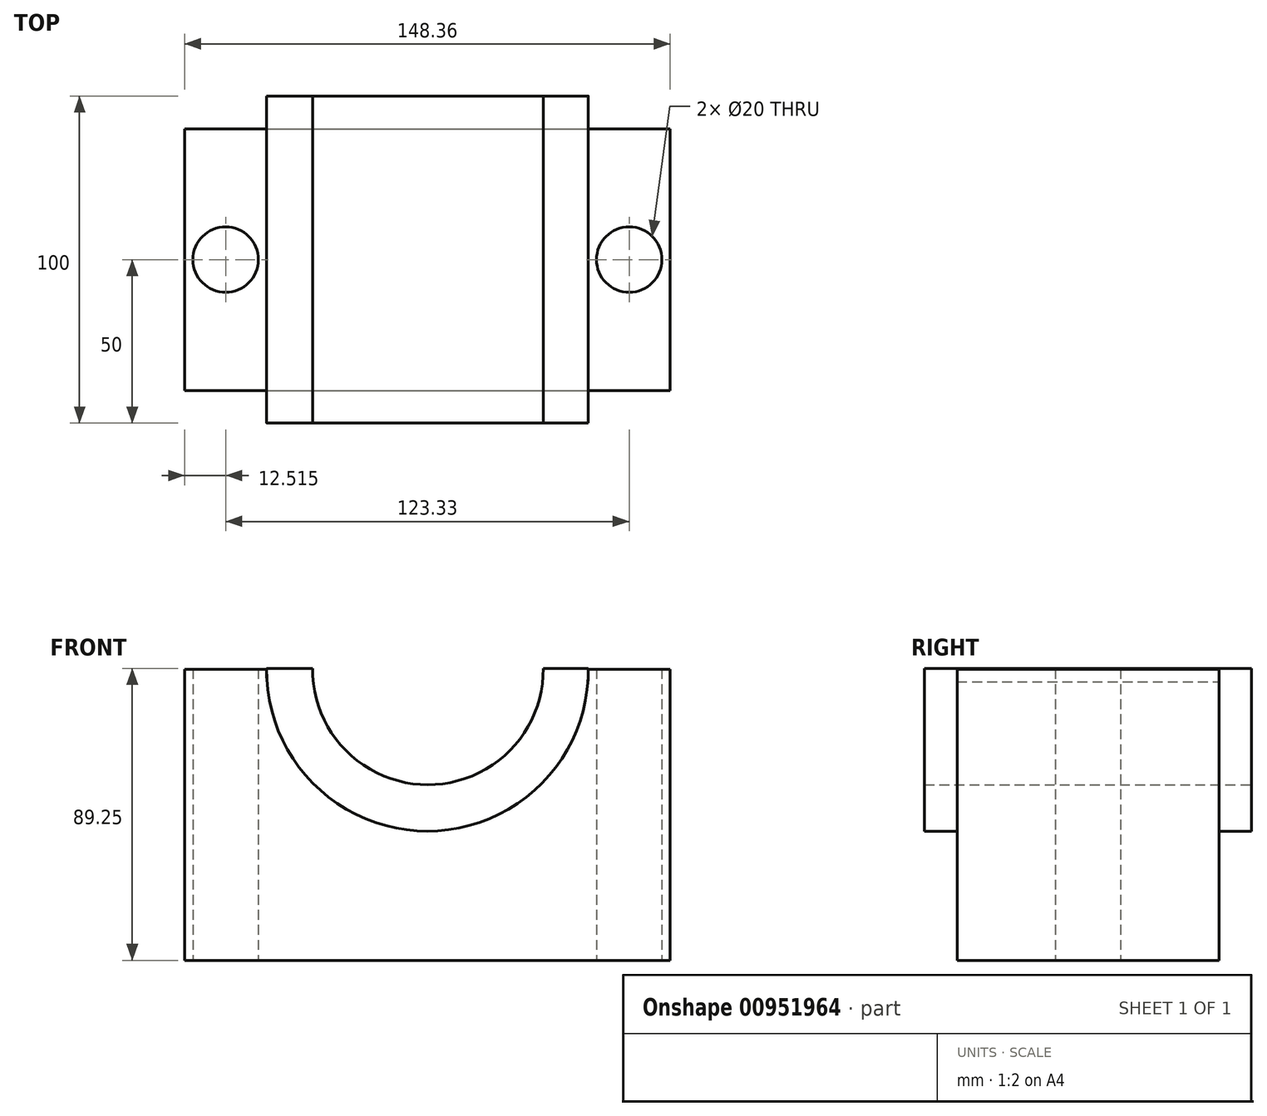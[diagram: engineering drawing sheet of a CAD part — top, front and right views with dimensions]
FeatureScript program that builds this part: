
annotation { "Feature Type Name" : "Feature", "Feature Type Description" : "" }
export const myFeature = defineFeature(function(context is Context, id is Id, definition is map)
    precondition{}
    {
        {
            var Q0;
            Q0=qCreatedBy(makeId("Front.planeOp"),FACE);
            var sketch = newSketch(context, id + "F0", { "sketchPlane" : qUnion([Q0])});
            skLineSegment(sketch, "E0.top", {"start": v(-74.18, -44.5) * mm, "end": v(74.18, -44.5) * mm});
            skLineSegment(sketch, "E0.left", {"start": v(-74.18, 44.5) * mm, "end": v(-74.18, -44.5) * mm});
            skLineSegment(sketch, "E0.right", {"start": v(74.18, 44.5) * mm, "end": v(74.18, -44.5) * mm});
            skArc(sketch, "E1", {"start": v(-35.24, 44.5) * mm, "mid": v(0, 9.26) * mm, "end": v(35.24, 44.5) * mm});
            skLineSegment(sketch, "E2", {"start": v(-74.18, 44.5) * mm, "end": v(-35.24, 44.5) * mm});
            skLineSegment(sketch, "E3", {"start": v(35.24, 44.5) * mm, "end": v(74.18, 44.5) * mm});
            skArc(sketch, "E4", {"start": v(-49.18, 44.5) * mm, "mid": v(0, -4.67) * mm, "end": v(49.18, 44.5) * mm});
            skSolve(sketch);
        }
        {
            var Q0;
            Q0=qCreatedBy(makeId("Front.planeOp"),FACE);
            var sketch = newSketch(context, id + "F1", { "sketchPlane" : qUnion([Q0])});
            skArc(sketch, "E5", {"start": v(-49.15, 44.74) * mm, "mid": v(0, -5) * mm, "end": v(49.15, 44.74) * mm});
            skArc(sketch, "E6", {"start": v(-35.1, 44.74) * mm, "mid": v(0.14, 9.17) * mm, "end": v(35.38, 44.74) * mm});
            skLineSegment(sketch, "E7", {"start": v(-35.1, 44.74) * mm, "end": v(-49.15, 44.74) * mm});
            skLineSegment(sketch, "E8", {"start": v(49.15, 44.74) * mm, "end": v(35.38, 44.74) * mm});
            skSolve(sketch);
        }
        {
            var Q0;
            Q0=makeQuery(id+"F0.imprint","IMPRINT",FACE,{"disambiguationData":[TD([[makeQuery(id+"F0.imprint","IMPRINT",EDGE,{"derivedFrom":sQuery(id+"F0.wireOp",EDGE,"E0.top")}),1.0]])]});
            extrude(context, id + "F2", {"entities" : qUnion([Q0]), "depth" : 80 * mm, "offsetDistance" : 25 * mm, "symmetric" : true});
        }
        {
            var Q0;
            Q0 = qSketchRegion(id + "F1", true);
            extrude(context, id + "F3", {"entities" : qUnion([Q0]), "operationType" : NewBodyOperationType.ADD, "depth" : 100 * mm, "offsetDistance" : 25 * mm, "symmetric" : true});
        }
        {
            var Q0;
            Q0=makeQuery(id+"F2.opExtrude","SWEPT_FACE",FACE,{"disambiguationData":[OSD([sQuery(id+"F0.wireOp",EDGE,"E0.top")])]});
            var sketch = newSketch(context, id + "F4", { "sketchPlane" : qUnion([Q0])});
            skLineSegment(sketch, "E9.bottom", {"start": v(-74.18, 40) * mm, "end": v(-49.15, 40) * mm});
            skLineSegment(sketch, "E9.top", {"start": v(-74.18, -40) * mm, "end": v(-49.15, -40) * mm});
            skLineSegment(sketch, "E9.left", {"start": v(-74.18, 40) * mm, "end": v(-74.18, -40) * mm});
            skLineSegment(sketch, "E9.right", {"start": v(-49.15, 40) * mm, "end": v(-49.15, -40) * mm});
            skLineSegment(sketch, "E10.bottom", {"start": v(49.15, -40) * mm, "end": v(74.18, -40) * mm});
            skLineSegment(sketch, "E10.top", {"start": v(49.15, 40) * mm, "end": v(74.18, 40) * mm});
            skLineSegment(sketch, "E10.left", {"start": v(49.15, -40) * mm, "end": v(49.15, 40) * mm});
            skLineSegment(sketch, "E10.right", {"start": v(74.18, -40) * mm, "end": v(74.18, 40) * mm});
            skPoint(sketch, "E11", {"position": v(-61.66, 0) * mm});
            skPoint(sketch, "E11.positionSnap0", {"position": v(-61.66, 40) * mm});
            skPoint(sketch, "E11.positionSnap1", {"position": v(-74.18, 0) * mm});
            skPoint(sketch, "E12", {"position": v(61.66, 0) * mm});
            skPoint(sketch, "E12.positionSnap0", {"position": v(61.66, 40) * mm});
            skSolve(sketch);
        }
        {
            var Q0;
            Q0=sQuery(id+"F4.wireOp",VERTEX,"E11");
            var Q1;
            Q1=sQuery(id+"F4.wireOp",VERTEX,"E12");
            var Q2;
            Q2=makeQuery(id+"F2.opExtrude","SWEPT_BODY",BODY,{"disambiguationData":[OSD([sQuery(id+"F0.wireOp",EDGE,"E0.top"),sQuery(id+"F0.wireOp",EDGE,"E0.left"),sQuery(id+"F0.wireOp",EDGE,"E0.right"),sQuery(id+"F0.wireOp",EDGE,"E2"),sQuery(id+"F0.wireOp",EDGE,"E3"),sQuery(id+"F0.wireOp",EDGE,"E4")])]});
            hole(context, id + "F5", {"style" : HoleStyle.SIMPLE, "endStyle" : HoleEndStyle.THROUGH, "holeDiameter" : 20 * mm, "majorDiameter" : 5 * mm, "isTappedThrough" : true, "tappedDepth" : 12 * mm, "tapClearance" : 3, "locations" : qUnion([Q0, Q1]), "scope" : qUnion([Q2])});
        }
    });
